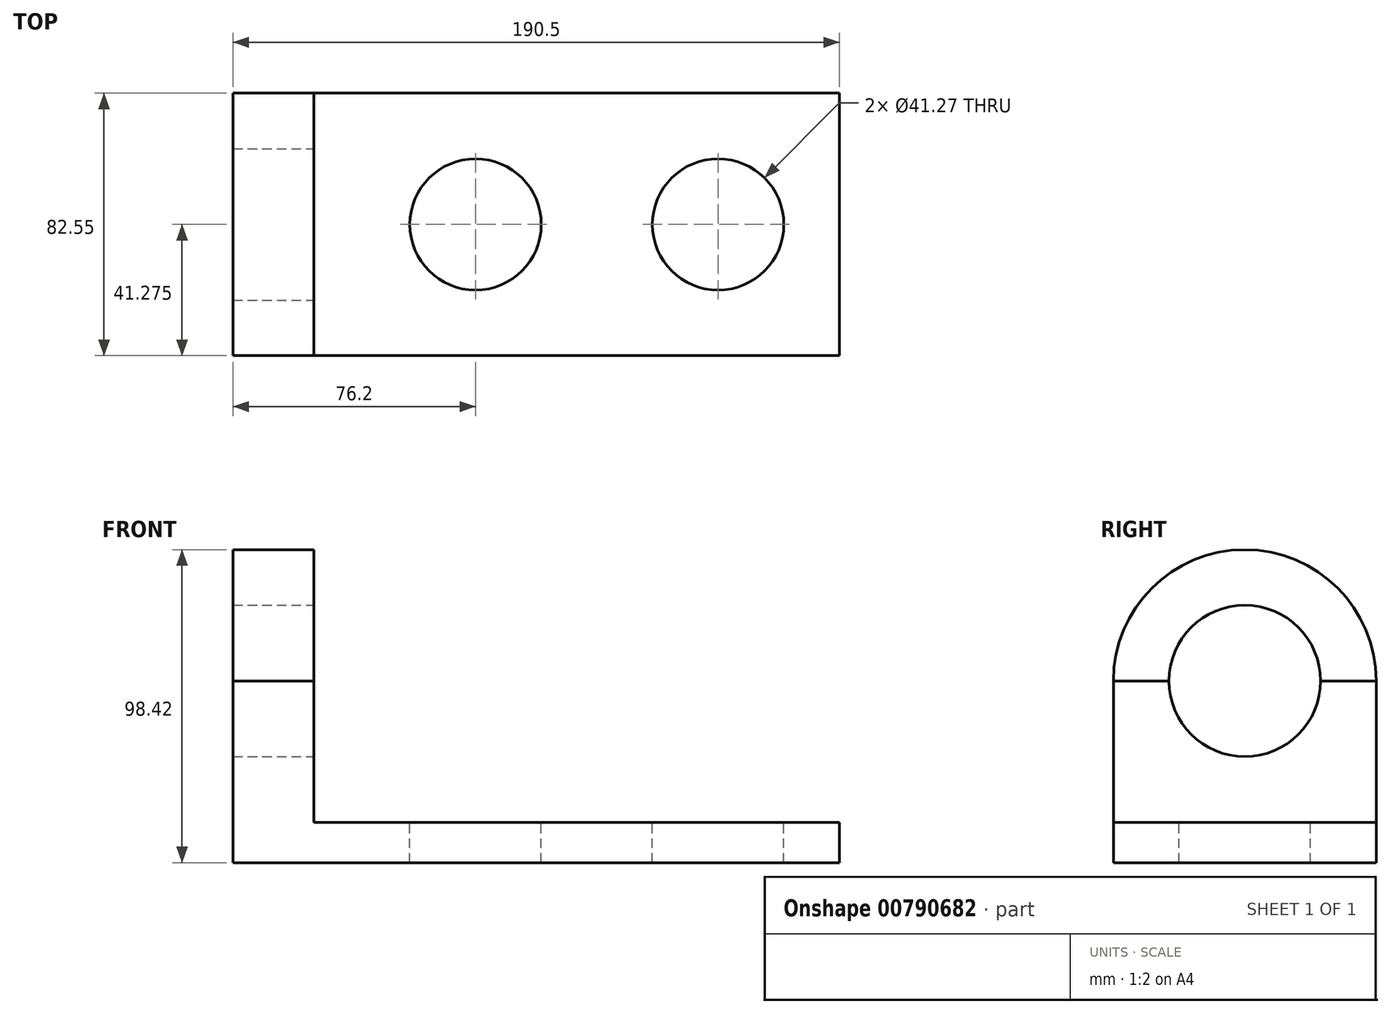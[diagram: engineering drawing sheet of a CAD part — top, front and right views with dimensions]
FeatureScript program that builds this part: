
annotation { "Feature Type Name" : "Feature", "Feature Type Description" : "" }
export const myFeature = defineFeature(function(context is Context, id is Id, definition is map)
    precondition{}
    {
        {
            var Q0;
            Q0=qCreatedBy(makeId("Front.planeOp"),FACE);
            var sketch = newSketch(context, id + "F0", { "sketchPlane" : qUnion([Q0])});
            skLineSegment(sketch, "E0", {"start": v(0, 0) * mm, "end": v(190.5, 0) * mm});
            skLineSegment(sketch, "E1", {"start": v(190.5, 0) * mm, "end": v(190.5, 12.7) * mm});
            skLineSegment(sketch, "E2", {"start": v(190.5, 12.7) * mm, "end": v(25.4, 12.7) * mm});
            skLineSegment(sketch, "E3", {"start": v(25.4, 12.7) * mm, "end": v(25.4, 57.15) * mm});
            skLineSegment(sketch, "E4", {"start": v(25.4, 57.15) * mm, "end": v(0, 57.15) * mm});
            skLineSegment(sketch, "E5", {"start": v(0, 57.15) * mm, "end": v(0, 0) * mm});
            skSolve(sketch);
        }
        {
            var Q0;
            Q0=makeQuery(id+"F0.imprint","IMPRINT",FACE,{"disambiguationData":[TD([[makeQuery(id+"F0.imprint","IMPRINT",EDGE,{"derivedFrom":sQuery(id+"F0.wireOp",EDGE,"E0")}),1.0]])]});
            extrude(context, id + "F1", {"entities" : qUnion([Q0]), "depth" : 82.55 * mm, "offsetDistance" : 25.4 * mm});
        }
        {
            var Q0;
            Q0=makeQuery(id+"F1.opExtrude","SWEPT_FACE",FACE,{"disambiguationData":[OSD([sQuery(id+"F0.wireOp",EDGE,"E2")])]});
            var sketch = newSketch(context, id + "F2", { "sketchPlane" : qUnion([Q0])});
            skLineSegment(sketch, "E6", {"start": v(190.5, -41.28) * mm, "end": v(152.4, -41.28) * mm, "construction": true});
            skLineSegment(sketch, "E7", {"start": v(152.4, -41.28) * mm, "end": v(76.2, -41.28) * mm, "construction": true});
            skCircle(sketch, "E8", {"center": v(152.4, -41.28) * mm, "radius": 20.64 * mm});
            skCircle(sketch, "E9", {"center": v(76.2, -41.28) * mm, "radius": 20.64 * mm});
            skSolve(sketch);
        }
        {
            var Q0;
            Q0=makeQuery(id+"F2.imprint","IMPRINT",FACE,{"disambiguationData":[TD([[makeQuery(id+"F2.imprint","IMPRINT",EDGE,{"derivedFrom":sQuery(id+"F2.wireOp",EDGE,"E9")}),1.0]])]});
            var Q1;
            Q1=makeQuery(id+"F2.imprint","IMPRINT",FACE,{"disambiguationData":[TD([[makeQuery(id+"F2.imprint","IMPRINT",EDGE,{"derivedFrom":sQuery(id+"F2.wireOp",EDGE,"E8")}),1.0]])]});
            extrude(context, id + "F3", {"entities" : qUnion([Q0, Q1]), "operationType" : NewBodyOperationType.REMOVE, "endBound" : BoundingType.THROUGH_ALL, "oppositeDirection" : true, "depth" : 25.4 * mm, "offsetDistance" : 25.4 * mm});
        }
        {
            var Q0;
            Q0=makeQuery(id+"F1.opExtrude","SWEPT_FACE",FACE,{"disambiguationData":[OSD([sQuery(id+"F0.wireOp",EDGE,"E3")])]});
            var sketch = newSketch(context, id + "F4", { "sketchPlane" : qUnion([Q0])});
            skArc(sketch, "E10", {"start": v(0, 57.15) * mm, "mid": v(-41.28, 98.42) * mm, "end": v(-82.55, 57.15) * mm});
            skSolve(sketch);
        }
        {
            var Q0;
            Q0=makeQuery(id+"F4.imprint","IMPRINT",FACE,{"disambiguationData":[TD([[makeQuery(id+"F4.imprint","IMPRINT",EDGE,{"derivedFrom":sQuery(id+"F4.wireOp",EDGE,"E10")}),1.0]])]});
            extrude(context, id + "F5", {"entities" : qUnion([Q0]), "oppositeDirection" : true, "depth" : 25.4 * mm, "offsetDistance" : 25.4 * mm});
        }
        {
            var Q0;
            Q0=makeQuery(id+"F5.opExtrude","CAP_FACE",FACE,{"disambiguationData":[OSD([sQuery(id+"F0.wireOp",EDGE,"E3"),sQuery(id+"F0.wireOp",EDGE,"E4"),sQuery(id+"F4.wireOp",EDGE,"E10")])],"isStart":true});
            var sketch = newSketch(context, id + "F6", { "sketchPlane" : qUnion([Q0])});
            skCircle(sketch, "E11", {"center": v(-41.28, 57.15) * mm, "radius": 23.81 * mm});
            skSolve(sketch);
        }
        {
            var Q0;
            {var subQ0=sQuery(id+"F6.wireOp",EDGE,"E11");var subQ1=makeQuery(id+"F5.opExtrude","CAP_EDGE",EDGE,{"disambiguationData":[OSD([sQuery(id+"F0.wireOp",EDGE,"E3"),sQuery(id+"F0.wireOp",EDGE,"E4")])],"isStart":true});var subQ2=makeQuery(id+"F6.imprint","INTERSECT",VERTEX,{"disambiguationData":[OD(0.0)],"derivedFrom":[subQ1,subQ0]});Q0=makeQuery(id+"F6.imprint","IMPRINT",FACE,{"disambiguationData":[TD([[makeQuery(id+"F6.imprint","IMPRINT",EDGE,{"disambiguationData":[TD([[subQ2,1.0]])],"derivedFrom":subQ0}),1.0]])]});}
            extrude(context, id + "F7", {"entities" : qUnion([Q0]), "operationType" : NewBodyOperationType.REMOVE, "endBound" : BoundingType.THROUGH_ALL, "oppositeDirection" : true, "depth" : 25.4 * mm, "offsetDistance" : 25.4 * mm});
        }
        {
            var Q0;
            Q0=makeQuery(id+"F5.opExtrude","CAP_FACE",FACE,{"disambiguationData":[OSD([sQuery(id+"F0.wireOp",EDGE,"E3"),sQuery(id+"F0.wireOp",EDGE,"E4"),sQuery(id+"F4.wireOp",EDGE,"E10")])],"isStart":true});
            var sketch = newSketch(context, id + "F8", { "sketchPlane" : qUnion([Q0])});
            skCircle(sketch, "E12", {"center": v(-41.28, 57.15) * mm, "radius": 23.81 * mm});
            skSolve(sketch);
        }
        {
            var Q0;
            {var subQ0=sQuery(id+"F8.wireOp",EDGE,"E12");var subQ1=makeQuery(id+"F5.opExtrude","CAP_EDGE",EDGE,{"disambiguationData":[OSD([sQuery(id+"F0.wireOp",EDGE,"E3"),sQuery(id+"F0.wireOp",EDGE,"E4")])],"isStart":true});var subQ2=makeQuery(id+"F8.imprint","INTERSECT",VERTEX,{"disambiguationData":[OD(0.0)],"derivedFrom":[subQ1,subQ0]});Q0=makeQuery(id+"F8.imprint","IMPRINT",FACE,{"disambiguationData":[TD([[makeQuery(id+"F8.imprint","IMPRINT",EDGE,{"disambiguationData":[TD([[subQ2,-1.0]])],"derivedFrom":subQ0}),1.0]])]});}
            extrude(context, id + "F9", {"entities" : qUnion([Q0]), "operationType" : NewBodyOperationType.REMOVE, "endBound" : BoundingType.THROUGH_ALL, "oppositeDirection" : true, "depth" : 25.4 * mm, "offsetDistance" : 25.4 * mm});
        }
    });
